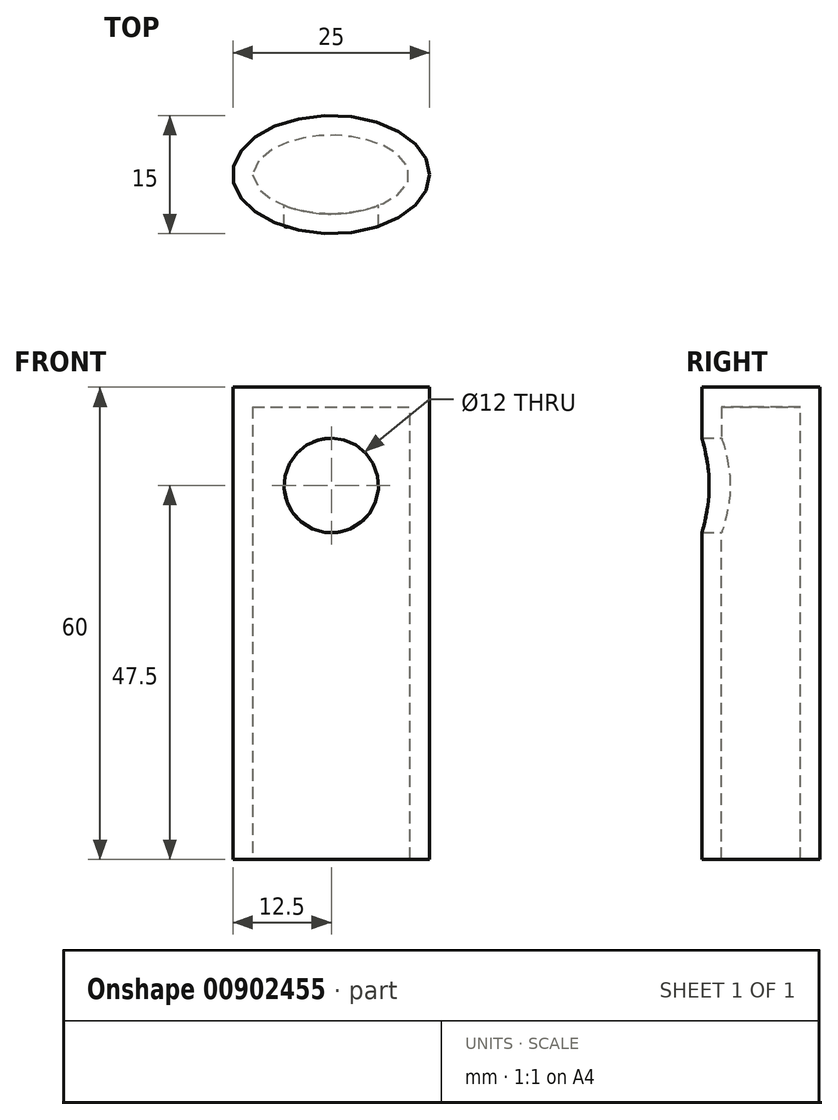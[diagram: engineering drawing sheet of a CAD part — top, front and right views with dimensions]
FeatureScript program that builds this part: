
annotation { "Feature Type Name" : "Feature", "Feature Type Description" : "" }
export const myFeature = defineFeature(function(context is Context, id is Id, definition is map)
    precondition{}
    {
        {
            var Q0;
            Q0=qCreatedBy(makeId("Top.planeOp"),FACE);
            var sketch = newSketch(context, id + "F0", { "sketchPlane" : qUnion([Q0])});
            skEllipse(sketch, "E0", {"center": v(0, 0) * mm, "majorRadius": 12.5 * mm, "minorRadius": 7.5 * mm, "majorAxis": v(1, 0)});
            skSolve(sketch);
        }
        {
            var Q0;
            Q0 = qSketchRegion(id + "F0", true);
            extrude(context, id + "F1", {"entities" : qUnion([Q0]), "depth" : 60 * mm, "offsetDistance" : 25 * mm});
        }
        {
            var Q0;
            Q0=makeQuery(id+"F1.opExtrude","CAP_FACE",FACE,{"disambiguationData":[OSD([sQuery(id+"F0.wireOp",EDGE,"E0")])],"isStart":true});
            shell(context, id + "F2", {"entities" : qUnion([Q0]), "thickness" : 2.5 * mm});
        }
        {
            var Q0;
            Q0=qCreatedBy(makeId("Front.planeOp"),FACE);
            var sketch = newSketch(context, id + "F3", { "sketchPlane" : qUnion([Q0])});
            skLineSegment(sketch, "E1", {"start": v(0, 0) * mm, "end": v(0, 60) * mm, "construction": true});
            skLineSegment(sketch, "E2", {"start": v(0, 60) * mm, "end": v(-22.38, 60) * mm, "construction": true});
            skLineSegment(sketch, "E3.0", {"start": v(0, 47.5) * mm, "end": v(-22.38, 47.5) * mm});
            skCircle(sketch, "E4", {"center": v(0, 47.5) * mm, "radius": 6 * mm});
            skSolve(sketch);
        }
        {
            var Q0;
            Q0 = qSketchRegion(id + "F3", true);
            extrude(context, id + "F4", {"entities" : qUnion([Q0]), "operationType" : NewBodyOperationType.REMOVE, "depth" : 25 * mm, "offsetDistance" : 25 * mm});
        }
    });
